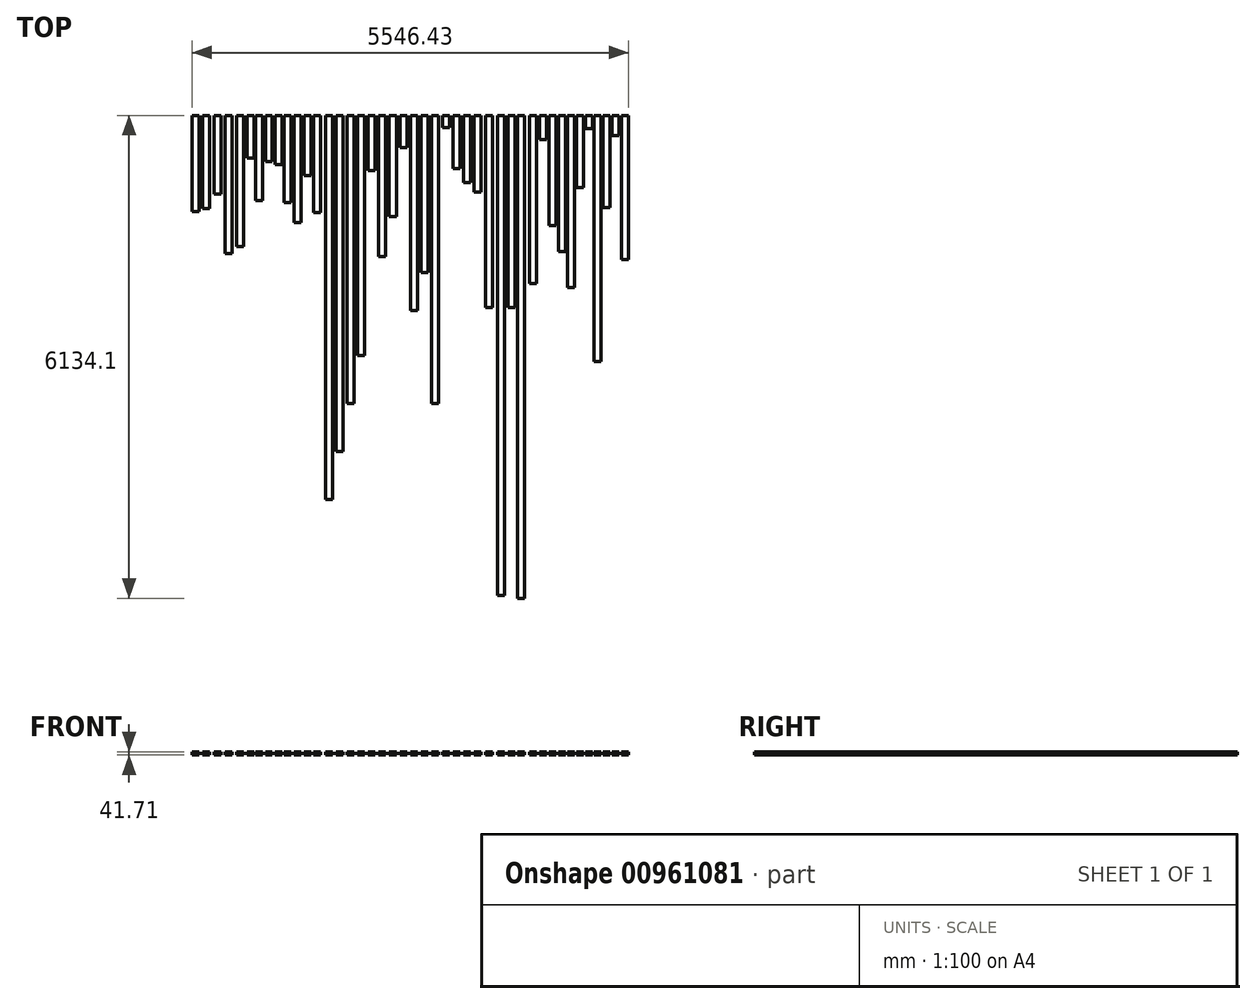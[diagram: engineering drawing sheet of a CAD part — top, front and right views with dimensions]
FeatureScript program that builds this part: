
annotation { "Feature Type Name" : "Feature", "Feature Type Description" : "" }
export const myFeature = defineFeature(function(context is Context, id is Id, definition is map)
    precondition{}
    {
        {
            var Q0;
            Q0=qCreatedBy(makeId("Front.planeOp"),FACE);
            var sketch = newSketch(context, id + "F0", { "sketchPlane" : qUnion([Q0])});
            skLineSegment(sketch, "E0.bottom", {"start": v(44.45, 19.05) * mm, "end": v(-44.45, 19.05) * mm});
            skLineSegment(sketch, "E0.top", {"start": v(44.45, -19.05) * mm, "end": v(-44.45, -19.05) * mm});
            skLineSegment(sketch, "E0.left", {"start": v(44.45, 19.05) * mm, "end": v(44.45, -19.05) * mm});
            skLineSegment(sketch, "E0.right", {"start": v(-44.45, 19.05) * mm, "end": v(-44.45, -19.05) * mm});
            skPoint(sketch, "E0.middle", {"position": v(0, 0) * mm});
            skLineSegment(sketch, "E1.1.0.0", {"start": v(90.42, 19.05) * mm, "end": v(90.42, -19.05) * mm});
            skLineSegment(sketch, "E1.1.0.1", {"start": v(179.32, 19.05) * mm, "end": v(90.42, 19.05) * mm});
            skLineSegment(sketch, "E1.1.0.2", {"start": v(179.32, -19.05) * mm, "end": v(90.42, -19.05) * mm});
            skLineSegment(sketch, "E1.1.0.3", {"start": v(179.32, 19.05) * mm, "end": v(179.32, -19.05) * mm});
            skLineSegment(sketch, "E1.2.0.0", {"start": v(225.3, 19.05) * mm, "end": v(225.3, -19.05) * mm});
            skLineSegment(sketch, "E1.2.0.1", {"start": v(314.2, 19.05) * mm, "end": v(225.3, 19.05) * mm});
            skLineSegment(sketch, "E1.2.0.2", {"start": v(314.2, -19.05) * mm, "end": v(225.3, -19.05) * mm});
            skLineSegment(sketch, "E1.2.0.3", {"start": v(314.2, 19.05) * mm, "end": v(314.2, -19.05) * mm});
            skLineSegment(sketch, "E1.3.0.0", {"start": v(360.17, 19.05) * mm, "end": v(360.17, -19.05) * mm});
            skLineSegment(sketch, "E1.3.0.1", {"start": v(449.07, 19.05) * mm, "end": v(360.17, 19.05) * mm});
            skLineSegment(sketch, "E1.3.0.2", {"start": v(449.07, -19.05) * mm, "end": v(360.17, -19.05) * mm});
            skLineSegment(sketch, "E1.3.0.3", {"start": v(449.07, 19.05) * mm, "end": v(449.07, -19.05) * mm});
            skLineSegment(sketch, "E1.4.0.0", {"start": v(495.05, 19.05) * mm, "end": v(495.05, -19.05) * mm});
            skLineSegment(sketch, "E1.4.0.1", {"start": v(583.95, 19.05) * mm, "end": v(495.05, 19.05) * mm});
            skLineSegment(sketch, "E1.4.0.2", {"start": v(583.95, -19.05) * mm, "end": v(495.05, -19.05) * mm});
            skLineSegment(sketch, "E1.4.0.3", {"start": v(583.95, 19.05) * mm, "end": v(583.95, -19.05) * mm});
            skLineSegment(sketch, "E1.5.0.0", {"start": v(629.92, 19.05) * mm, "end": v(629.92, -19.05) * mm});
            skLineSegment(sketch, "E1.5.0.1", {"start": v(718.82, 19.05) * mm, "end": v(629.92, 19.05) * mm});
            skLineSegment(sketch, "E1.5.0.2", {"start": v(718.82, -19.05) * mm, "end": v(629.92, -19.05) * mm});
            skLineSegment(sketch, "E1.5.0.3", {"start": v(718.82, 19.05) * mm, "end": v(718.82, -19.05) * mm});
            skLineSegment(sketch, "E1.direction1", {"start": v(-44.45, -19.05) * mm, "end": v(90.42, -19.05) * mm, "construction": true});
            skLineSegment(sketch, "E2.0.6.0", {"start": v(764.8, 19.05) * mm, "end": v(764.8, -19.05) * mm});
            skLineSegment(sketch, "E2.3.6.0", {"start": v(853.7, 19.05) * mm, "end": v(764.8, 19.05) * mm});
            skLineSegment(sketch, "E2.6.6.0", {"start": v(853.7, -19.05) * mm, "end": v(764.8, -19.05) * mm});
            skLineSegment(sketch, "E2.9.6.0", {"start": v(853.7, 19.05) * mm, "end": v(853.7, -19.05) * mm});
            skLineSegment(sketch, "E2.0.7.0", {"start": v(899.67, 19.05) * mm, "end": v(899.67, -19.05) * mm});
            skLineSegment(sketch, "E2.3.7.0", {"start": v(988.57, 19.05) * mm, "end": v(899.67, 19.05) * mm});
            skLineSegment(sketch, "E2.6.7.0", {"start": v(988.57, -19.05) * mm, "end": v(899.67, -19.05) * mm});
            skLineSegment(sketch, "E2.9.7.0", {"start": v(988.57, 19.05) * mm, "end": v(988.57, -19.05) * mm});
            skLineSegment(sketch, "E2.0.8.0", {"start": v(1034.54, 19.05) * mm, "end": v(1034.54, -19.05) * mm});
            skLineSegment(sketch, "E2.3.8.0", {"start": v(1123.44, 19.05) * mm, "end": v(1034.54, 19.05) * mm});
            skLineSegment(sketch, "E2.6.8.0", {"start": v(1123.44, -19.05) * mm, "end": v(1034.54, -19.05) * mm});
            skLineSegment(sketch, "E2.9.8.0", {"start": v(1123.44, 19.05) * mm, "end": v(1123.44, -19.05) * mm});
            skLineSegment(sketch, "E2.0.9.0", {"start": v(1169.42, 19.05) * mm, "end": v(1169.42, -19.05) * mm});
            skLineSegment(sketch, "E2.3.9.0", {"start": v(1258.32, 19.05) * mm, "end": v(1169.42, 19.05) * mm});
            skLineSegment(sketch, "E2.6.9.0", {"start": v(1258.32, -19.05) * mm, "end": v(1169.42, -19.05) * mm});
            skLineSegment(sketch, "E2.9.9.0", {"start": v(1258.32, 19.05) * mm, "end": v(1258.32, -19.05) * mm});
            skLineSegment(sketch, "E3.0.10.0", {"start": v(1304.29, 19.05) * mm, "end": v(1304.29, -19.05) * mm});
            skLineSegment(sketch, "E3.3.10.0", {"start": v(1393.19, 19.05) * mm, "end": v(1304.29, 19.05) * mm});
            skLineSegment(sketch, "E3.6.10.0", {"start": v(1393.19, -19.05) * mm, "end": v(1304.29, -19.05) * mm});
            skLineSegment(sketch, "E3.9.10.0", {"start": v(1393.19, 19.05) * mm, "end": v(1393.19, -19.05) * mm});
            skLineSegment(sketch, "E3.0.11.0", {"start": v(1439.16, 19.05) * mm, "end": v(1439.16, -19.05) * mm});
            skLineSegment(sketch, "E3.3.11.0", {"start": v(1528.06, 19.05) * mm, "end": v(1439.16, 19.05) * mm});
            skLineSegment(sketch, "E3.6.11.0", {"start": v(1528.06, -19.05) * mm, "end": v(1439.16, -19.05) * mm});
            skLineSegment(sketch, "E3.9.11.0", {"start": v(1528.06, 19.05) * mm, "end": v(1528.06, -19.05) * mm});
            skLineSegment(sketch, "E3.0.12.0", {"start": v(1574.04, 19.05) * mm, "end": v(1574.04, -19.05) * mm});
            skLineSegment(sketch, "E3.3.12.0", {"start": v(1662.94, 19.05) * mm, "end": v(1574.04, 19.05) * mm});
            skLineSegment(sketch, "E3.6.12.0", {"start": v(1662.94, -19.05) * mm, "end": v(1574.04, -19.05) * mm});
            skLineSegment(sketch, "E3.9.12.0", {"start": v(1662.94, 19.05) * mm, "end": v(1662.94, -19.05) * mm});
            skLineSegment(sketch, "E3.0.13.0", {"start": v(1708.91, 19.05) * mm, "end": v(1708.91, -19.05) * mm});
            skLineSegment(sketch, "E3.3.13.0", {"start": v(1797.81, 19.05) * mm, "end": v(1708.91, 19.05) * mm});
            skLineSegment(sketch, "E3.6.13.0", {"start": v(1797.81, -19.05) * mm, "end": v(1708.91, -19.05) * mm});
            skLineSegment(sketch, "E3.9.13.0", {"start": v(1797.81, 19.05) * mm, "end": v(1797.81, -19.05) * mm});
            skLineSegment(sketch, "E3.0.14.0", {"start": v(1843.79, 19.05) * mm, "end": v(1843.79, -19.05) * mm});
            skLineSegment(sketch, "E3.3.14.0", {"start": v(1932.69, 19.05) * mm, "end": v(1843.79, 19.05) * mm});
            skLineSegment(sketch, "E3.6.14.0", {"start": v(1932.69, -19.05) * mm, "end": v(1843.79, -19.05) * mm});
            skLineSegment(sketch, "E3.9.14.0", {"start": v(1932.69, 19.05) * mm, "end": v(1932.69, -19.05) * mm});
            skLineSegment(sketch, "E4.bottom", {"start": v(1988.08, 17.42) * mm, "end": v(2076.98, 17.42) * mm});
            skLineSegment(sketch, "E4.top", {"start": v(1988.08, -20.68) * mm, "end": v(2076.98, -20.68) * mm});
            skLineSegment(sketch, "E4.left", {"start": v(1988.08, 17.42) * mm, "end": v(1988.08, -20.68) * mm});
            skLineSegment(sketch, "E4.right", {"start": v(2076.98, 17.42) * mm, "end": v(2076.98, -20.68) * mm});
            skLineSegment(sketch, "E5.bottom", {"start": v(2139.93, 17.66) * mm, "end": v(2228.83, 17.66) * mm});
            skLineSegment(sketch, "E5.top", {"start": v(2139.93, -20.44) * mm, "end": v(2228.83, -20.44) * mm});
            skLineSegment(sketch, "E5.left", {"start": v(2139.93, 17.66) * mm, "end": v(2139.93, -20.44) * mm});
            skLineSegment(sketch, "E5.right", {"start": v(2228.83, 17.66) * mm, "end": v(2228.83, -20.44) * mm});
            skLineSegment(sketch, "E6.bottom", {"start": v(2271.52, 20.17) * mm, "end": v(2360.42, 20.17) * mm});
            skLineSegment(sketch, "E6.top", {"start": v(2271.52, -17.93) * mm, "end": v(2360.42, -17.93) * mm});
            skLineSegment(sketch, "E6.left", {"start": v(2271.52, 20.17) * mm, "end": v(2271.52, -17.93) * mm});
            skLineSegment(sketch, "E6.right", {"start": v(2360.42, 20.17) * mm, "end": v(2360.42, -17.93) * mm});
            skLineSegment(sketch, "E7.bottom", {"start": v(2395.44, 20.17) * mm, "end": v(2484.34, 20.17) * mm});
            skLineSegment(sketch, "E7.top", {"start": v(2395.44, -17.93) * mm, "end": v(2484.34, -17.93) * mm});
            skLineSegment(sketch, "E7.left", {"start": v(2395.44, 20.17) * mm, "end": v(2395.44, -17.93) * mm});
            skLineSegment(sketch, "E7.right", {"start": v(2484.34, 20.17) * mm, "end": v(2484.34, -17.93) * mm});
            skLineSegment(sketch, "E8.bottom", {"start": v(2545.3, 20.17) * mm, "end": v(2634.2, 20.17) * mm});
            skLineSegment(sketch, "E8.top", {"start": v(2545.3, -17.93) * mm, "end": v(2634.2, -17.93) * mm});
            skLineSegment(sketch, "E8.left", {"start": v(2545.3, 20.17) * mm, "end": v(2545.3, -17.93) * mm});
            skLineSegment(sketch, "E8.right", {"start": v(2634.2, 20.17) * mm, "end": v(2634.2, -17.93) * mm});
            skLineSegment(sketch, "E9.bottom", {"start": v(2675.52, 20.17) * mm, "end": v(2764.42, 20.17) * mm});
            skLineSegment(sketch, "E9.top", {"start": v(2675.52, -17.93) * mm, "end": v(2764.42, -17.93) * mm});
            skLineSegment(sketch, "E9.left", {"start": v(2675.52, 20.17) * mm, "end": v(2675.52, -17.93) * mm});
            skLineSegment(sketch, "E9.right", {"start": v(2764.42, 20.17) * mm, "end": v(2764.42, -17.93) * mm});
            skLineSegment(sketch, "E10.bottom", {"start": v(2790.94, 20.17) * mm, "end": v(2879.84, 20.17) * mm});
            skLineSegment(sketch, "E10.top", {"start": v(2790.94, -17.93) * mm, "end": v(2879.84, -17.93) * mm});
            skLineSegment(sketch, "E10.left", {"start": v(2790.94, 20.17) * mm, "end": v(2790.94, -17.93) * mm});
            skLineSegment(sketch, "E10.right", {"start": v(2879.84, 20.17) * mm, "end": v(2879.84, -17.93) * mm});
            skLineSegment(sketch, "E11.bottom", {"start": v(2911.4, 20.17) * mm, "end": v(3000.3, 20.17) * mm});
            skLineSegment(sketch, "E11.top", {"start": v(2911.4, -17.93) * mm, "end": v(3000.3, -17.93) * mm});
            skLineSegment(sketch, "E11.left", {"start": v(2911.4, 20.17) * mm, "end": v(2911.4, -17.93) * mm});
            skLineSegment(sketch, "E11.right", {"start": v(3000.3, 20.17) * mm, "end": v(3000.3, -17.93) * mm});
            skLineSegment(sketch, "E12.bottom", {"start": v(-107.3, 17.66) * mm, "end": v(-196.2, 17.66) * mm});
            skLineSegment(sketch, "E12.top", {"start": v(-107.3, -20.44) * mm, "end": v(-196.2, -20.44) * mm});
            skLineSegment(sketch, "E12.left", {"start": v(-107.3, 17.66) * mm, "end": v(-107.3, -20.44) * mm});
            skLineSegment(sketch, "E12.right", {"start": v(-196.2, 17.66) * mm, "end": v(-196.2, -20.44) * mm});
            skPoint(sketch, "E12.middle", {"position": v(-151.76, -1.39) * mm});
            skLineSegment(sketch, "E13.bottom", {"start": v(-230.64, 17.3) * mm, "end": v(-319.54, 17.3) * mm});
            skLineSegment(sketch, "E13.top", {"start": v(-230.64, -20.8) * mm, "end": v(-319.54, -20.8) * mm});
            skLineSegment(sketch, "E13.left", {"start": v(-230.64, 17.3) * mm, "end": v(-230.64, -20.8) * mm});
            skLineSegment(sketch, "E13.right", {"start": v(-319.54, 17.3) * mm, "end": v(-319.54, -20.8) * mm});
            skPoint(sketch, "E13.middle", {"position": v(-275.1, -1.74) * mm});
            skLineSegment(sketch, "E14.bottom", {"start": v(-354.96, 17.69) * mm, "end": v(-443.86, 17.69) * mm});
            skLineSegment(sketch, "E14.top", {"start": v(-354.96, -20.41) * mm, "end": v(-443.86, -20.41) * mm});
            skLineSegment(sketch, "E14.left", {"start": v(-354.96, 17.69) * mm, "end": v(-354.96, -20.41) * mm});
            skLineSegment(sketch, "E14.right", {"start": v(-443.86, 17.69) * mm, "end": v(-443.86, -20.41) * mm});
            skPoint(sketch, "E14.middle", {"position": v(-399.4, -1.36) * mm});
            skLineSegment(sketch, "E15.bottom", {"start": v(-480.58, 19.66) * mm, "end": v(-569.48, 19.66) * mm});
            skLineSegment(sketch, "E15.top", {"start": v(-480.58, -18.44) * mm, "end": v(-569.48, -18.44) * mm});
            skLineSegment(sketch, "E15.left", {"start": v(-480.58, 19.66) * mm, "end": v(-480.58, -18.44) * mm});
            skLineSegment(sketch, "E15.right", {"start": v(-569.48, 19.66) * mm, "end": v(-569.48, -18.44) * mm});
            skPoint(sketch, "E15.middle", {"position": v(-525.03, 0.6) * mm});
            skLineSegment(sketch, "E16.bottom", {"start": v(-599.6, 20.17) * mm, "end": v(-688.5, 20.17) * mm});
            skLineSegment(sketch, "E16.top", {"start": v(-599.6, -17.93) * mm, "end": v(-688.5, -17.93) * mm});
            skLineSegment(sketch, "E16.left", {"start": v(-599.6, 20.17) * mm, "end": v(-599.6, -17.93) * mm});
            skLineSegment(sketch, "E16.right", {"start": v(-688.5, 20.17) * mm, "end": v(-688.5, -17.93) * mm});
            skPoint(sketch, "E16.middle", {"position": v(-644.04, 1.12) * mm});
            skLineSegment(sketch, "E17.bottom", {"start": v(-720.84, 17.7) * mm, "end": v(-809.74, 17.7) * mm});
            skLineSegment(sketch, "E17.top", {"start": v(-720.84, -20.4) * mm, "end": v(-809.74, -20.4) * mm});
            skLineSegment(sketch, "E17.left", {"start": v(-720.84, 17.7) * mm, "end": v(-720.84, -20.4) * mm});
            skLineSegment(sketch, "E17.right", {"start": v(-809.74, 17.7) * mm, "end": v(-809.74, -20.4) * mm});
            skPoint(sketch, "E17.middle", {"position": v(-765.3, -1.35) * mm});
            skLineSegment(sketch, "E18.bottom", {"start": v(-844.46, 19.05) * mm, "end": v(-933.36, 19.05) * mm});
            skLineSegment(sketch, "E18.top", {"start": v(-844.46, -19.05) * mm, "end": v(-933.36, -19.05) * mm});
            skLineSegment(sketch, "E18.left", {"start": v(-844.46, 19.05) * mm, "end": v(-844.46, -19.05) * mm});
            skLineSegment(sketch, "E18.right", {"start": v(-933.36, 19.05) * mm, "end": v(-933.36, -19.05) * mm});
            skPoint(sketch, "E18.middle", {"position": v(-888.91, 0) * mm});
            skLineSegment(sketch, "E19.bottom", {"start": v(-955.38, 20.5) * mm, "end": v(-1044.28, 20.5) * mm});
            skLineSegment(sketch, "E19.top", {"start": v(-955.38, -17.6) * mm, "end": v(-1044.28, -17.6) * mm});
            skLineSegment(sketch, "E19.left", {"start": v(-955.38, 20.5) * mm, "end": v(-955.38, -17.6) * mm});
            skLineSegment(sketch, "E19.right", {"start": v(-1044.28, 20.5) * mm, "end": v(-1044.28, -17.6) * mm});
            skPoint(sketch, "E19.middle", {"position": v(-999.83, 1.45) * mm});
            skLineSegment(sketch, "E20.bottom", {"start": v(-1088.94, 19.98) * mm, "end": v(-1177.84, 19.98) * mm});
            skLineSegment(sketch, "E20.top", {"start": v(-1088.94, -18.12) * mm, "end": v(-1177.84, -18.12) * mm});
            skLineSegment(sketch, "E20.left", {"start": v(-1088.94, 19.98) * mm, "end": v(-1088.94, -18.12) * mm});
            skLineSegment(sketch, "E20.right", {"start": v(-1177.84, 19.98) * mm, "end": v(-1177.84, -18.12) * mm});
            skPoint(sketch, "E20.middle", {"position": v(-1133.4, 0.93) * mm});
            skLineSegment(sketch, "E21.bottom", {"start": v(-1231.5, 20.5) * mm, "end": v(-1320.4, 20.5) * mm});
            skLineSegment(sketch, "E21.top", {"start": v(-1231.5, -17.6) * mm, "end": v(-1320.4, -17.6) * mm});
            skLineSegment(sketch, "E21.left", {"start": v(-1231.5, 20.5) * mm, "end": v(-1231.5, -17.6) * mm});
            skLineSegment(sketch, "E21.right", {"start": v(-1320.4, 20.5) * mm, "end": v(-1320.4, -17.6) * mm});
            skPoint(sketch, "E21.middle", {"position": v(-1275.94, 1.45) * mm});
            skLineSegment(sketch, "E22.bottom", {"start": v(-1369.37, 20.92) * mm, "end": v(-1458.27, 20.92) * mm});
            skLineSegment(sketch, "E22.top", {"start": v(-1369.37, -17.18) * mm, "end": v(-1458.27, -17.18) * mm});
            skLineSegment(sketch, "E22.left", {"start": v(-1369.37, 20.92) * mm, "end": v(-1369.37, -17.18) * mm});
            skLineSegment(sketch, "E22.right", {"start": v(-1458.27, 20.92) * mm, "end": v(-1458.27, -17.18) * mm});
            skPoint(sketch, "E22.middle", {"position": v(-1413.82, 1.87) * mm});
            skLineSegment(sketch, "E23.bottom", {"start": v(-1517.8, 19.05) * mm, "end": v(-1606.7, 19.05) * mm});
            skLineSegment(sketch, "E23.top", {"start": v(-1517.8, -19.05) * mm, "end": v(-1606.7, -19.05) * mm});
            skLineSegment(sketch, "E23.left", {"start": v(-1517.8, 19.05) * mm, "end": v(-1517.8, -19.05) * mm});
            skLineSegment(sketch, "E23.right", {"start": v(-1606.7, 19.05) * mm, "end": v(-1606.7, -19.05) * mm});
            skPoint(sketch, "E23.middle", {"position": v(-1562.25, 0) * mm});
            skLineSegment(sketch, "E24.bottom", {"start": v(-1652.88, 19.98) * mm, "end": v(-1741.78, 19.98) * mm});
            skLineSegment(sketch, "E24.top", {"start": v(-1652.88, -18.12) * mm, "end": v(-1741.78, -18.12) * mm});
            skLineSegment(sketch, "E24.left", {"start": v(-1652.88, 19.98) * mm, "end": v(-1652.88, -18.12) * mm});
            skLineSegment(sketch, "E24.right", {"start": v(-1741.78, 19.98) * mm, "end": v(-1741.78, -18.12) * mm});
            skPoint(sketch, "E24.middle", {"position": v(-1697.33, 0.93) * mm});
            skLineSegment(sketch, "E25.bottom", {"start": v(3030.36, 17.3) * mm, "end": v(3119.26, 17.3) * mm});
            skLineSegment(sketch, "E25.top", {"start": v(3030.36, -20.8) * mm, "end": v(3119.26, -20.8) * mm});
            skLineSegment(sketch, "E25.left", {"start": v(3030.36, 17.3) * mm, "end": v(3030.36, -20.8) * mm});
            skLineSegment(sketch, "E25.right", {"start": v(3119.26, 17.3) * mm, "end": v(3119.26, -20.8) * mm});
            skLineSegment(sketch, "E26.bottom", {"start": v(3141.75, 17.7) * mm, "end": v(3230.65, 17.7) * mm});
            skLineSegment(sketch, "E26.top", {"start": v(3141.75, -20.4) * mm, "end": v(3230.65, -20.4) * mm});
            skLineSegment(sketch, "E26.left", {"start": v(3141.75, 17.7) * mm, "end": v(3141.75, -20.4) * mm});
            skLineSegment(sketch, "E26.right", {"start": v(3230.65, 17.7) * mm, "end": v(3230.65, -20.4) * mm});
            skLineSegment(sketch, "E27.bottom", {"start": v(3255.87, 20.92) * mm, "end": v(3344.77, 20.92) * mm});
            skLineSegment(sketch, "E27.top", {"start": v(3255.87, -17.18) * mm, "end": v(3344.77, -17.18) * mm});
            skLineSegment(sketch, "E27.left", {"start": v(3255.87, 20.92) * mm, "end": v(3255.87, -17.18) * mm});
            skLineSegment(sketch, "E27.right", {"start": v(3344.77, 20.92) * mm, "end": v(3344.77, -17.18) * mm});
            skLineSegment(sketch, "E28.bottom", {"start": v(3364.98, 20.92) * mm, "end": v(3453.88, 20.92) * mm});
            skLineSegment(sketch, "E28.top", {"start": v(3364.98, -17.18) * mm, "end": v(3453.88, -17.18) * mm});
            skLineSegment(sketch, "E28.left", {"start": v(3364.98, 20.92) * mm, "end": v(3364.98, -17.18) * mm});
            skLineSegment(sketch, "E28.right", {"start": v(3453.88, 20.92) * mm, "end": v(3453.88, -17.18) * mm});
            skLineSegment(sketch, "E29.bottom", {"start": v(3479.9, 20.92) * mm, "end": v(3568.8, 20.92) * mm});
            skLineSegment(sketch, "E29.top", {"start": v(3479.9, -17.18) * mm, "end": v(3568.8, -17.18) * mm});
            skLineSegment(sketch, "E29.left", {"start": v(3479.9, 20.92) * mm, "end": v(3479.9, -17.18) * mm});
            skLineSegment(sketch, "E29.right", {"start": v(3568.8, 20.92) * mm, "end": v(3568.8, -17.18) * mm});
            skLineSegment(sketch, "E30.bottom", {"start": v(3596.67, 20.92) * mm, "end": v(3685.57, 20.92) * mm});
            skLineSegment(sketch, "E30.top", {"start": v(3596.67, -17.18) * mm, "end": v(3685.57, -17.18) * mm});
            skLineSegment(sketch, "E30.left", {"start": v(3596.67, 20.92) * mm, "end": v(3596.67, -17.18) * mm});
            skLineSegment(sketch, "E30.right", {"start": v(3685.57, 20.92) * mm, "end": v(3685.57, -17.18) * mm});
            skLineSegment(sketch, "E31.bottom", {"start": v(3715.75, 20.92) * mm, "end": v(3804.65, 20.92) * mm});
            skLineSegment(sketch, "E31.top", {"start": v(3715.75, -17.18) * mm, "end": v(3804.65, -17.18) * mm});
            skLineSegment(sketch, "E31.left", {"start": v(3715.75, 20.92) * mm, "end": v(3715.75, -17.18) * mm});
            skLineSegment(sketch, "E31.right", {"start": v(3804.65, 20.92) * mm, "end": v(3804.65, -17.18) * mm});
            skSolve(sketch);
        }
        {
            var Q0;
            Q0=makeQuery(id+"F0.imprint","IMPRINT",FACE,{"disambiguationData":[TD([[makeQuery(id+"F0.imprint","IMPRINT",EDGE,{"derivedFrom":sQuery(id+"F0.wireOp",EDGE,"E7.bottom")}),-1.0]])]});
            extrude(context, id + "F1", {"entities" : qUnion([Q0]), "depth" : 6134.1 * mm, "offsetDistance" : 25.4 * mm});
        }
        {
            var Q0;
            Q0=makeQuery(id+"F0.imprint","IMPRINT",FACE,{"disambiguationData":[TD([[makeQuery(id+"F0.imprint","IMPRINT",EDGE,{"derivedFrom":sQuery(id+"F0.wireOp",EDGE,"E5.bottom")}),-1.0]])]});
            extrude(context, id + "F2", {"entities" : qUnion([Q0]), "depth" : 6096 * mm, "offsetDistance" : 25.4 * mm});
        }
        {
            var Q0;
            Q0=makeQuery(id+"F0.imprint","IMPRINT",FACE,{"disambiguationData":[TD([[makeQuery(id+"F0.imprint","IMPRINT",EDGE,{"derivedFrom":sQuery(id+"F0.wireOp",EDGE,"E0.bottom")}),1.0]])]});
            extrude(context, id + "F3", {"entities" : qUnion([Q0]), "depth" : 4876.8 * mm, "offsetDistance" : 25.4 * mm});
        }
        {
            var Q0;
            Q0=makeQuery(id+"F0.imprint","IMPRINT",FACE,{"disambiguationData":[TD([[makeQuery(id+"F0.imprint","IMPRINT",EDGE,{"derivedFrom":sQuery(id+"F0.wireOp",EDGE,"E1.1.0.0")}),1.0]])]});
            extrude(context, id + "F4", {"entities" : qUnion([Q0]), "depth" : 4267.2 * mm, "offsetDistance" : 25.4 * mm});
        }
        {
            var Q0;
            Q0=makeQuery(id+"F0.imprint","IMPRINT",FACE,{"disambiguationData":[TD([[makeQuery(id+"F0.imprint","IMPRINT",EDGE,{"derivedFrom":sQuery(id+"F0.wireOp",EDGE,"E1.2.0.0")}),1.0]])]});
            extrude(context, id + "F5", {"entities" : qUnion([Q0]), "depth" : 3657.6 * mm, "offsetDistance" : 25.4 * mm});
        }
        {
            var Q0;
            Q0=makeQuery(id+"F0.imprint","IMPRINT",FACE,{"disambiguationData":[TD([[makeQuery(id+"F0.imprint","IMPRINT",EDGE,{"derivedFrom":sQuery(id+"F0.wireOp",EDGE,"E3.0.10.0")}),1.0]])]});
            extrude(context, id + "F6", {"entities" : qUnion([Q0]), "depth" : 3657.6 * mm, "offsetDistance" : 25.4 * mm});
        }
        {
            var Q0;
            Q0=makeQuery(id+"F0.imprint","IMPRINT",FACE,{"disambiguationData":[TD([[makeQuery(id+"F0.imprint","IMPRINT",EDGE,{"derivedFrom":sQuery(id+"F0.wireOp",EDGE,"E28.bottom")}),-1.0]])]});
            extrude(context, id + "F7", {"entities" : qUnion([Q0]), "depth" : 3124.2 * mm, "offsetDistance" : 25.4 * mm});
        }
        {
            var Q0;
            Q0=makeQuery(id+"F0.imprint","IMPRINT",FACE,{"disambiguationData":[TD([[makeQuery(id+"F0.imprint","IMPRINT",EDGE,{"derivedFrom":sQuery(id+"F0.wireOp",EDGE,"E1.3.0.0")}),1.0]])]});
            extrude(context, id + "F8", {"entities" : qUnion([Q0]), "depth" : 3048 * mm, "offsetDistance" : 25.4 * mm});
        }
        {
            var Q0;
            Q0=makeQuery(id+"F0.imprint","IMPRINT",FACE,{"disambiguationData":[TD([[makeQuery(id+"F0.imprint","IMPRINT",EDGE,{"derivedFrom":sQuery(id+"F0.wireOp",EDGE,"E2.0.8.0")}),1.0]])]});
            extrude(context, id + "F9", {"entities" : qUnion([Q0]), "depth" : 2476.5 * mm, "offsetDistance" : 25.4 * mm});
        }
        {
            var Q0;
            Q0=makeQuery(id+"F0.imprint","IMPRINT",FACE,{"disambiguationData":[TD([[makeQuery(id+"F0.imprint","IMPRINT",EDGE,{"derivedFrom":sQuery(id+"F0.wireOp",EDGE,"E4.bottom")}),-1.0]])]});
            extrude(context, id + "F10", {"entities" : qUnion([Q0]), "depth" : 2438.4 * mm, "offsetDistance" : 25.4 * mm});
        }
        {
            var Q0;
            Q0=makeQuery(id+"F0.imprint","IMPRINT",FACE,{"disambiguationData":[TD([[makeQuery(id+"F0.imprint","IMPRINT",EDGE,{"derivedFrom":sQuery(id+"F0.wireOp",EDGE,"E6.bottom")}),-1.0]])]});
            extrude(context, id + "F11", {"entities" : qUnion([Q0]), "depth" : 2438.4 * mm, "offsetDistance" : 25.4 * mm});
        }
        {
            var Q0;
            Q0=makeQuery(id+"F0.imprint","IMPRINT",FACE,{"disambiguationData":[TD([[makeQuery(id+"F0.imprint","IMPRINT",EDGE,{"derivedFrom":sQuery(id+"F0.wireOp",EDGE,"E8.bottom")}),-1.0]])]});
            extrude(context, id + "F12", {"entities" : qUnion([Q0]), "depth" : 2133.6 * mm, "offsetDistance" : 25.4 * mm});
        }
        {
            var Q0;
            Q0=makeQuery(id+"F0.imprint","IMPRINT",FACE,{"disambiguationData":[TD([[makeQuery(id+"F0.imprint","IMPRINT",EDGE,{"derivedFrom":sQuery(id+"F0.wireOp",EDGE,"E25.bottom")}),-1.0]])]});
            extrude(context, id + "F13", {"entities" : qUnion([Q0]), "depth" : 2184.4 * mm, "offsetDistance" : 25.4 * mm});
        }
        {
            var Q0;
            Q0=makeQuery(id+"F0.imprint","IMPRINT",FACE,{"disambiguationData":[TD([[makeQuery(id+"F0.imprint","IMPRINT",EDGE,{"derivedFrom":sQuery(id+"F0.wireOp",EDGE,"E2.0.9.0")}),1.0]])]});
            extrude(context, id + "F14", {"entities" : qUnion([Q0]), "depth" : 1993.9 * mm, "offsetDistance" : 25.4 * mm});
        }
        {
            var Q0;
            Q0=makeQuery(id+"F0.imprint","IMPRINT",FACE,{"disambiguationData":[TD([[makeQuery(id+"F0.imprint","IMPRINT",EDGE,{"derivedFrom":sQuery(id+"F0.wireOp",EDGE,"E31.bottom")}),-1.0]])]});
            extrude(context, id + "F15", {"entities" : qUnion([Q0]), "depth" : 1828.8 * mm, "offsetDistance" : 25.4 * mm});
        }
        {
            var Q0;
            Q0=makeQuery(id+"F0.imprint","IMPRINT",FACE,{"disambiguationData":[TD([[makeQuery(id+"F0.imprint","IMPRINT",EDGE,{"derivedFrom":sQuery(id+"F0.wireOp",EDGE,"E1.5.0.0")}),1.0]])]});
            extrude(context, id + "F16", {"entities" : qUnion([Q0]), "depth" : 1790.7 * mm, "offsetDistance" : 25.4 * mm});
        }
        {
            var Q0;
            Q0=makeQuery(id+"F0.imprint","IMPRINT",FACE,{"disambiguationData":[TD([[makeQuery(id+"F0.imprint","IMPRINT",EDGE,{"derivedFrom":sQuery(id+"F0.wireOp",EDGE,"E21.bottom")}),1.0]])]});
            extrude(context, id + "F17", {"entities" : qUnion([Q0]), "depth" : 1752.6 * mm, "offsetDistance" : 25.4 * mm});
        }
        {
            var Q0;
            Q0=makeQuery(id+"F0.imprint","IMPRINT",FACE,{"disambiguationData":[TD([[makeQuery(id+"F0.imprint","IMPRINT",EDGE,{"derivedFrom":sQuery(id+"F0.wireOp",EDGE,"E11.bottom")}),-1.0]])]});
            extrude(context, id + "F18", {"entities" : qUnion([Q0]), "depth" : 1727.2 * mm, "offsetDistance" : 25.4 * mm});
        }
        {
            var Q0;
            Q0=makeQuery(id+"F0.imprint","IMPRINT",FACE,{"disambiguationData":[TD([[makeQuery(id+"F0.imprint","IMPRINT",EDGE,{"derivedFrom":sQuery(id+"F0.wireOp",EDGE,"E20.bottom")}),1.0]])]});
            extrude(context, id + "F19", {"entities" : qUnion([Q0]), "depth" : 1663.7 * mm, "offsetDistance" : 25.4 * mm});
        }
        {
            var Q0;
            Q0=makeQuery(id+"F0.imprint","IMPRINT",FACE,{"disambiguationData":[TD([[makeQuery(id+"F0.imprint","IMPRINT",EDGE,{"derivedFrom":sQuery(id+"F0.wireOp",EDGE,"E10.bottom")}),-1.0]])]});
            extrude(context, id + "F20", {"entities" : qUnion([Q0]), "depth" : 1397 * mm, "offsetDistance" : 25.4 * mm});
        }
        {
            var Q0;
            Q0=makeQuery(id+"F0.imprint","IMPRINT",FACE,{"disambiguationData":[TD([[makeQuery(id+"F0.imprint","IMPRINT",EDGE,{"derivedFrom":sQuery(id+"F0.wireOp",EDGE,"E14.bottom")}),1.0]])]});
            extrude(context, id + "F21", {"entities" : qUnion([Q0]), "depth" : 1363.47 * mm, "offsetDistance" : 25.4 * mm});
        }
        {
            var Q0;
            Q0=makeQuery(id+"F0.imprint","IMPRINT",FACE,{"disambiguationData":[TD([[makeQuery(id+"F0.imprint","IMPRINT",EDGE,{"derivedFrom":sQuery(id+"F0.wireOp",EDGE,"E2.0.6.0")}),1.0]])]});
            extrude(context, id + "F22", {"entities" : qUnion([Q0]), "depth" : 1282.7 * mm, "offsetDistance" : 25.4 * mm});
        }
        {
            var Q0;
            Q0=makeQuery(id+"F0.imprint","IMPRINT",FACE,{"disambiguationData":[TD([[makeQuery(id+"F0.imprint","IMPRINT",EDGE,{"derivedFrom":sQuery(id+"F0.wireOp",EDGE,"E12.bottom")}),1.0]])]});
            extrude(context, id + "F23", {"entities" : qUnion([Q0]), "depth" : 1234.44 * mm, "offsetDistance" : 25.4 * mm});
        }
        {
            var Q0;
            Q0=makeQuery(id+"F0.imprint","IMPRINT",FACE,{"disambiguationData":[TD([[makeQuery(id+"F0.imprint","IMPRINT",EDGE,{"derivedFrom":sQuery(id+"F0.wireOp",EDGE,"E24.bottom")}),1.0]])]});
            extrude(context, id + "F24", {"entities" : qUnion([Q0]), "depth" : 1219.2 * mm, "offsetDistance" : 25.4 * mm});
        }
        {
            var Q0;
            Q0=makeQuery(id+"F0.imprint","IMPRINT",FACE,{"disambiguationData":[TD([[makeQuery(id+"F0.imprint","IMPRINT",EDGE,{"derivedFrom":sQuery(id+"F0.wireOp",EDGE,"E23.bottom")}),1.0]])]});
            extrude(context, id + "F25", {"entities" : qUnion([Q0]), "depth" : 1181.1 * mm, "offsetDistance" : 25.4 * mm});
        }
        {
            var Q0;
            Q0=makeQuery(id+"F0.imprint","IMPRINT",FACE,{"disambiguationData":[TD([[makeQuery(id+"F0.imprint","IMPRINT",EDGE,{"derivedFrom":sQuery(id+"F0.wireOp",EDGE,"E29.bottom")}),-1.0]])]});
            extrude(context, id + "F26", {"entities" : qUnion([Q0]), "depth" : 1168.4 * mm, "offsetDistance" : 25.4 * mm});
        }
        {
            var Q0;
            Q0=makeQuery(id+"F0.imprint","IMPRINT",FACE,{"disambiguationData":[TD([[makeQuery(id+"F0.imprint","IMPRINT",EDGE,{"derivedFrom":sQuery(id+"F0.wireOp",EDGE,"E15.bottom")}),1.0]])]});
            extrude(context, id + "F27", {"entities" : qUnion([Q0]), "depth" : 1104.9 * mm, "offsetDistance" : 25.4 * mm});
        }
        {
            var Q0;
            Q0=makeQuery(id+"F0.imprint","IMPRINT",FACE,{"disambiguationData":[TD([[makeQuery(id+"F0.imprint","IMPRINT",EDGE,{"derivedFrom":sQuery(id+"F0.wireOp",EDGE,"E18.bottom")}),1.0]])]});
            extrude(context, id + "F28", {"entities" : qUnion([Q0]), "depth" : 1079.5 * mm, "offsetDistance" : 25.4 * mm});
        }
        {
            var Q0;
            Q0=makeQuery(id+"F0.imprint","IMPRINT",FACE,{"disambiguationData":[TD([[makeQuery(id+"F0.imprint","IMPRINT",EDGE,{"derivedFrom":sQuery(id+"F0.wireOp",EDGE,"E22.bottom")}),1.0]])]});
            extrude(context, id + "F29", {"entities" : qUnion([Q0]), "depth" : 998.22 * mm, "offsetDistance" : 25.4 * mm});
        }
        {
            var Q0;
            Q0=makeQuery(id+"F0.imprint","IMPRINT",FACE,{"disambiguationData":[TD([[makeQuery(id+"F0.imprint","IMPRINT",EDGE,{"derivedFrom":sQuery(id+"F0.wireOp",EDGE,"E3.0.14.0")}),1.0]])]});
            extrude(context, id + "F30", {"entities" : qUnion([Q0]), "depth" : 971.55 * mm, "offsetDistance" : 25.4 * mm});
        }
        {
            var Q0;
            Q0=makeQuery(id+"F0.imprint","IMPRINT",FACE,{"disambiguationData":[TD([[makeQuery(id+"F0.imprint","IMPRINT",EDGE,{"derivedFrom":sQuery(id+"F0.wireOp",EDGE,"E26.bottom")}),-1.0]])]});
            extrude(context, id + "F31", {"entities" : qUnion([Q0]), "depth" : 914.4 * mm, "offsetDistance" : 25.4 * mm});
        }
        {
            var Q0;
            Q0=makeQuery(id+"F0.imprint","IMPRINT",FACE,{"disambiguationData":[TD([[makeQuery(id+"F0.imprint","IMPRINT",EDGE,{"derivedFrom":sQuery(id+"F0.wireOp",EDGE,"E3.0.13.0")}),1.0]])]});
            extrude(context, id + "F32", {"entities" : qUnion([Q0]), "depth" : 854.07 * mm, "offsetDistance" : 25.4 * mm});
        }
        {
            var Q0;
            Q0=makeQuery(id+"F0.imprint","IMPRINT",FACE,{"disambiguationData":[TD([[makeQuery(id+"F0.imprint","IMPRINT",EDGE,{"derivedFrom":sQuery(id+"F0.wireOp",EDGE,"E13.bottom")}),1.0]])]});
            extrude(context, id + "F33", {"entities" : qUnion([Q0]), "depth" : 762 * mm, "offsetDistance" : 25.4 * mm});
        }
        {
            var Q0;
            Q0=makeQuery(id+"F0.imprint","IMPRINT",FACE,{"disambiguationData":[TD([[makeQuery(id+"F0.imprint","IMPRINT",EDGE,{"derivedFrom":sQuery(id+"F0.wireOp",EDGE,"E1.4.0.0")}),1.0]])]});
            extrude(context, id + "F34", {"entities" : qUnion([Q0]), "depth" : 698.5 * mm, "offsetDistance" : 25.4 * mm});
        }
        {
            var Q0;
            Q0=makeQuery(id+"F0.imprint","IMPRINT",FACE,{"disambiguationData":[TD([[makeQuery(id+"F0.imprint","IMPRINT",EDGE,{"derivedFrom":sQuery(id+"F0.wireOp",EDGE,"E3.0.12.0")}),1.0]])]});
            extrude(context, id + "F35", {"entities" : qUnion([Q0]), "depth" : 676.27 * mm, "offsetDistance" : 25.4 * mm});
        }
        {
            var Q0;
            Q0=makeQuery(id+"F0.imprint","IMPRINT",FACE,{"disambiguationData":[TD([[makeQuery(id+"F0.imprint","IMPRINT",EDGE,{"derivedFrom":sQuery(id+"F0.wireOp",EDGE,"E16.bottom")}),1.0]])]});
            extrude(context, id + "F36", {"entities" : qUnion([Q0]), "depth" : 622.3 * mm, "offsetDistance" : 25.4 * mm});
        }
        {
            var Q0;
            Q0=makeQuery(id+"F0.imprint","IMPRINT",FACE,{"disambiguationData":[TD([[makeQuery(id+"F0.imprint","IMPRINT",EDGE,{"derivedFrom":sQuery(id+"F0.wireOp",EDGE,"E17.bottom")}),1.0]])]});
            extrude(context, id + "F37", {"entities" : qUnion([Q0]), "depth" : 584.2 * mm, "offsetDistance" : 25.4 * mm});
        }
        {
            var Q0;
            Q0=makeQuery(id+"F0.imprint","IMPRINT",FACE,{"disambiguationData":[TD([[makeQuery(id+"F0.imprint","IMPRINT",EDGE,{"derivedFrom":sQuery(id+"F0.wireOp",EDGE,"E19.bottom")}),1.0]])]});
            extrude(context, id + "F38", {"entities" : qUnion([Q0]), "depth" : 544.58 * mm, "offsetDistance" : 25.4 * mm});
        }
        {
            var Q0;
            Q0=makeQuery(id+"F0.imprint","IMPRINT",FACE,{"disambiguationData":[TD([[makeQuery(id+"F0.imprint","IMPRINT",EDGE,{"derivedFrom":sQuery(id+"F0.wireOp",EDGE,"E2.0.7.0")}),1.0]])]});
            extrude(context, id + "F39", {"entities" : qUnion([Q0]), "depth" : 406.4 * mm, "offsetDistance" : 25.4 * mm});
        }
        {
            var Q0;
            Q0=makeQuery(id+"F0.imprint","IMPRINT",FACE,{"disambiguationData":[TD([[makeQuery(id+"F0.imprint","IMPRINT",EDGE,{"derivedFrom":sQuery(id+"F0.wireOp",EDGE,"E9.bottom")}),-1.0]])]});
            extrude(context, id + "F40", {"entities" : qUnion([Q0]), "depth" : 304.8 * mm, "offsetDistance" : 25.4 * mm});
        }
        {
            var Q0;
            Q0=makeQuery(id+"F0.imprint","IMPRINT",FACE,{"disambiguationData":[TD([[makeQuery(id+"F0.imprint","IMPRINT",EDGE,{"derivedFrom":sQuery(id+"F0.wireOp",EDGE,"E30.bottom")}),-1.0]])]});
            extrude(context, id + "F41", {"entities" : qUnion([Q0]), "depth" : 254 * mm, "offsetDistance" : 25.4 * mm});
        }
        {
            var Q0;
            Q0=makeQuery(id+"F0.imprint","IMPRINT",FACE,{"disambiguationData":[TD([[makeQuery(id+"F0.imprint","IMPRINT",EDGE,{"derivedFrom":sQuery(id+"F0.wireOp",EDGE,"E27.bottom")}),-1.0]])]});
            extrude(context, id + "F42", {"entities" : qUnion([Q0]), "depth" : 165.1 * mm, "offsetDistance" : 25.4 * mm});
        }
        {
            var Q0;
            Q0=makeQuery(id+"F0.imprint","IMPRINT",FACE,{"disambiguationData":[TD([[makeQuery(id+"F0.imprint","IMPRINT",EDGE,{"derivedFrom":sQuery(id+"F0.wireOp",EDGE,"E3.0.11.0")}),1.0]])]});
            extrude(context, id + "F43", {"entities" : qUnion([Q0]), "depth" : 152.4 * mm, "offsetDistance" : 25.4 * mm});
        }
        {
            var Q0;
            Q0=makeQuery(id+"F4.opExtrude","SWEPT_BODY",BODY,{"disambiguationData":[OSD([sQuery(id+"F0.wireOp",EDGE,"E1.1.0.0"),sQuery(id+"F0.wireOp",EDGE,"E1.1.0.1"),sQuery(id+"F0.wireOp",EDGE,"E1.1.0.2"),sQuery(id+"F0.wireOp",EDGE,"E1.1.0.3")])]});
            transform(context, id + "F44", {"entities" : qUnion([Q0]), "transformType" : TransformType.TRANSLATION_3D, "dx" : 0 * mm, "dy" : 0 * mm, "dz" : 0 * mm, "makeCopy" : true});
        }
        {
            var Q0;
            Q0=makeQuery(id+"F5.opExtrude","SWEPT_BODY",BODY,{"disambiguationData":[OSD([sQuery(id+"F0.wireOp",EDGE,"E1.2.0.0"),sQuery(id+"F0.wireOp",EDGE,"E1.2.0.1"),sQuery(id+"F0.wireOp",EDGE,"E1.2.0.2"),sQuery(id+"F0.wireOp",EDGE,"E1.2.0.3")])]});
            transform(context, id + "F45", {"entities" : qUnion([Q0]), "transformType" : TransformType.TRANSLATION_3D, "dx" : 0 * mm, "dy" : 0 * mm, "dz" : 0 * mm, "makeCopy" : true});
        }
    });
